FCSTD DOCUMENT  (FreeCAD 0.20R29410 (Git))
Label: ferris-left
License: All rights reserved
LicenseURL: http://en.wikipedia.org/wiki/All_rights_reserved
objects: Sketcher::SketchObject×1, PartDesign::Body×1
note: 2 computed .brp shape members not serialized (recipe doc carries the construction recipe); baked Part::Feature solids carry a one-line shape summary decoded from their .brp

FEATURE [Sketcher::SketchObject] Sketch
  FullyConstrained = false
  MapMode = 5
  Support = -> [XY_Plane]
  sketch-geometry (18):
    g0: ArcOfCircle CenterX=17.631 CenterY=-33.357 CenterZ=0 NormalX=0 NormalY=0 NormalZ=1 AngleXU=0 Radius=4.45635 StartAngle=2.38718 EndAngle=2.83085
    g1: ArcOfCircle CenterX=56.7327 CenterY=-76.9421 CenterZ=0 NormalX=0 NormalY=0 NormalZ=1 AngleXU=0 Radius=62.9956 StartAngle=1.97509 EndAngle=2.30804
    g2: ArcOfCircle CenterX=60.2954 CenterY=-81.9875 CenterZ=0 NormalX=0 NormalY=0 NormalZ=1 AngleXU=0 Radius=69.0478 StartAngle=1.46233 EndAngle=1.99378
    g3: ArcOfCircle CenterX=53.064 CenterY=-152.605 CenterZ=0 NormalX=0 NormalY=0 NormalZ=1 AngleXU=0 Radius=140.034 StartAngle=1.21601 EndAngle=1.46559
    g4: ArcOfCircle CenterX=101.585 CenterY=-22.093 CenterZ=0 NormalX=0 NormalY=0 NormalZ=1 AngleXU=0 Radius=0.810491 StartAngle=0.0304793 EndAngle=1.41626
    g5: LineSegment StartX=102.395 StartY=-22.0683 StartZ=0 EndX=102.395 EndY=-46.2654 EndZ=0
    g6: ArcOfCircle CenterX=105.039 CenterY=-45.3982 CenterZ=0 NormalX=0 NormalY=0 NormalZ=1 AngleXU=0 Radius=2.78192 StartAngle=3.45861 EndAngle=4.493
    g7: LineSegment StartX=104.433 StartY=-48.1134 StartZ=0 EndX=112.539 EndY=-48.1134 EndZ=0
    g8: ArcOfCircle CenterX=112.768 CenterY=-49.0696 CenterZ=0 NormalX=0 NormalY=0 NormalZ=1 AngleXU=0 Radius=0.983019 StartAngle=6.24758 EndAngle=8.08838
    g9: LineSegment StartX=113.75 StartY=-49.1046 StartZ=0 EndX=113.75 EndY=-81.9388 EndZ=0
    g10: ArcOfCircle CenterX=75.0792 CenterY=-80.0755 CenterZ=0 NormalX=0 NormalY=0 NormalZ=1 AngleXU=0 Radius=38.7158 StartAngle=6.1204 EndAngle=6.23504
    g11: LineSegment StartX=113.283 StartY=-86.35 StartZ=0 EndX=111.27 EndY=-99.137 EndZ=0
    g12: ArcOfCircle CenterX=108.896 CenterY=-98.4839 CenterZ=0 NormalX=0 NormalY=0 NormalZ=1 AngleXU=0 Radius=2.46234 StartAngle=4.2382 EndAngle=6.01477
    g13: ArcOfCircle CenterX=61.2837 CenterY=-179.585 CenterZ=0 NormalX=0 NormalY=0 NormalZ=1 AngleXU=0 Radius=91.5864 StartAngle=1.03841 EndAngle=1.31723
    g14: ArcOfCircle CenterX=26.0679 CenterY=-341.809 CenterZ=0 NormalX=0 NormalY=0 NormalZ=1 AngleXU=0 Radius=257.542 StartAngle=1.34288 EndAngle=1.48681
    g15: ArcOfCircle CenterX=7.51396 CenterY=-522.392 CenterZ=0 NormalX=0 NormalY=0 NormalZ=1 AngleXU=0 Radius=439.058 StartAngle=1.4792 EndAngle=1.55219
    g16: ArcOfCircle CenterX=15.8516 CenterY=-80.918 CenterZ=0 NormalX=0 NormalY=0 NormalZ=1 AngleXU=0 Radius=2.49844 StartAngle=3.3089 EndAngle=4.64503
    g17: LineSegment StartX=13.388 StartY=-31.9944 StartZ=0 EndX=13.388 EndY=-81.3341 EndZ=0
  constraints (22):
    c: Coincident(g1,g0)
    c: Coincident(g2,g1)
    c: Coincident(g3,g2)
    c: Coincident(g4,g3)
    c: Coincident(g5,g4)
    c: Vertical(g5)
    c: Coincident(g6,g5)
    c: Coincident(g7,g6)
    c: Horizontal(g7)
    c: Coincident(g8,g7)
    c: Coincident(g9,g8)
    c: Vertical(g9)
    c: Coincident(g10,g9)
    c: Coincident(g11,g10)
    c: Coincident(g12,g11)
    c: Coincident(g13,g12)
    c: Coincident(g14,g13)
    c: Coincident(g15,g14)
    c: Coincident(g16,g15)
    c: Coincident(g17,g0)
    c: Coincident(g17,g16)
    c: Vertical(g17)
FEATURE [PartDesign::Body] Body
  Group = -> [Sketch]
  Origin = -> Origin
